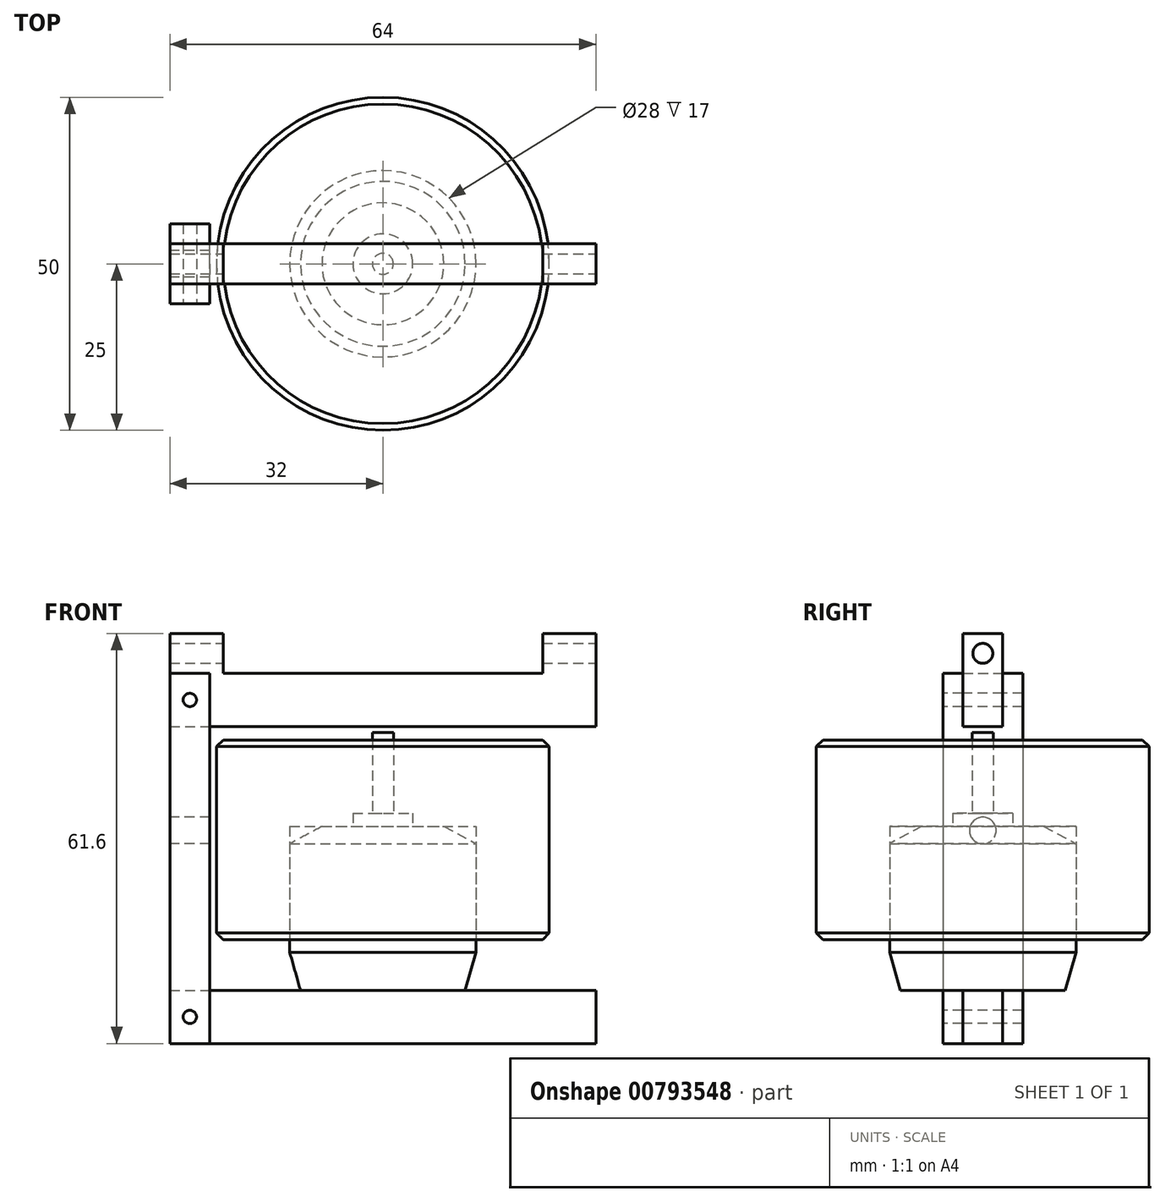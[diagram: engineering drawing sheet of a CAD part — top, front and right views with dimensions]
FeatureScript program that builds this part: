
annotation { "Feature Type Name" : "Feature", "Feature Type Description" : "" }
export const myFeature = defineFeature(function(context is Context, id is Id, definition is map)
    precondition{}
    {
        {
            var Q0;
            Q0=qCreatedBy(makeId("Right.planeOp"),FACE);
            var sketch = newSketch(context, id + "F0", { "sketchPlane" : qUnion([Q0])});
            skLineSegment(sketch, "E0", {"start": v(0, 0) * mm, "end": v(0, 26.6) * mm, "construction": true});
            skLineSegment(sketch, "E1", {"start": v(0, 26.6) * mm, "end": v(4.5, 26.6) * mm});
            skLineSegment(sketch, "E2", {"start": v(4.5, 26.6) * mm, "end": v(4.5, 24.6) * mm});
            skLineSegment(sketch, "E3", {"start": v(4.5, 24.6) * mm, "end": v(9.15, 24.6) * mm});
            skLineSegment(sketch, "E4", {"start": v(9.15, 24.6) * mm, "end": v(14, 22) * mm});
            skLineSegment(sketch, "E5", {"start": v(14, 22) * mm, "end": v(14, 5.7) * mm});
            skLineSegment(sketch, "E6", {"start": v(14, 5.7) * mm, "end": v(12.38, 0) * mm});
            skLineSegment(sketch, "E7", {"start": v(12.38, 0) * mm, "end": v(0, 0) * mm});
            skLineSegment(sketch, "E8", {"start": v(0, 26.6) * mm, "end": v(0, 0) * mm});
            skSolve(sketch);
        }
        {
            var Q0;
            Q0 = qSketchRegion(id + "F0", true);
            var Q1;
            Q1=sQuery(id+"F0.wireOp",EDGE,"E0");
            revolve(context, id + "F1", {"surfaceOperationType" : NewSurfaceOperationType.NEW, "entities" : qUnion([Q0]), "axis" : qUnion([Q1]), "revolveType" : RevolveType.FULL});
        }
        {
            var Q0;
            Q0=makeQuery(id+"F1.opRevolve","SWEPT_FACE",FACE,{"disambiguationData":[OSD([sQuery(id+"F0.wireOp",EDGE,"E1")])]});
            var sketch = newSketch(context, id + "F2", { "sketchPlane" : qUnion([Q0])});
            skCircle(sketch, "E9", {"center": v(0, 0) * mm, "radius": 1.59 * mm});
            skSolve(sketch);
        }
        {
            var Q0;
            Q0 = qSketchRegion(id + "F2", true);
            extrude(context, id + "F3", {"entities" : qUnion([Q0]), "operationType" : NewBodyOperationType.ADD, "depth" : 12.1 * mm, "offsetDistance" : 25 * mm});
        }
        {
            var Q0;
            Q0=qCreatedBy(makeId("Right.planeOp"),FACE);
            var sketch = newSketch(context, id + "F4", { "sketchPlane" : qUnion([Q0])});
            skLineSegment(sketch, "E10", {"start": v(0, 0) * mm, "end": v(0, 38.7) * mm, "construction": true});
            skLineSegment(sketch, "E11", {"start": v(1.58, 37.6) * mm, "end": v(1.59, 26.6) * mm});
            skLineSegment(sketch, "E12", {"start": v(1.59, 26.6) * mm, "end": v(4.5, 26.6) * mm});
            skLineSegment(sketch, "E13", {"start": v(14, 24.6) * mm, "end": v(14, 7.6) * mm});
            skLineSegment(sketch, "E14", {"start": v(14, 7.6) * mm, "end": v(25, 7.6) * mm});
            skLineSegment(sketch, "E15", {"start": v(25, 7.6) * mm, "end": v(25, 37.6) * mm});
            skLineSegment(sketch, "E16", {"start": v(25, 37.6) * mm, "end": v(1.58, 37.6) * mm});
            skLineSegment(sketch, "E17", {"start": v(4.5, 26.6) * mm, "end": v(4.5, 24.6) * mm});
            skLineSegment(sketch, "E18", {"start": v(4.5, 24.6) * mm, "end": v(14, 24.6) * mm});
            skSolve(sketch);
        }
        {
            var Q0;
            Q0 = qSketchRegion(id + "F4", true);
            var Q1;
            Q1=sQuery(id+"F4.wireOp",EDGE,"E10");
            revolve(context, id + "F5", {"surfaceOperationType" : NewSurfaceOperationType.NEW, "entities" : qUnion([Q0]), "axis" : qUnion([Q1]), "revolveType" : RevolveType.FULL});
        }
        {
            var Q0;
            Q0=makeQuery(id+"F5.opRevolve","SWEPT_EDGE",EDGE,{"disambiguationData":[OSD([sQuery(id+"F4.wireOp",EDGE,"E15"),sQuery(id+"F4.wireOp",EDGE,"E16")])]});
            var Q1;
            Q1=makeQuery(id+"F5.opRevolve","SWEPT_EDGE",EDGE,{"disambiguationData":[OSD([sQuery(id+"F4.wireOp",EDGE,"E14"),sQuery(id+"F4.wireOp",EDGE,"E15")])]});
            chamfer(context, id + "F6", {"entities" : qUnion([Q0, Q1]), "width" : 1 * mm, "tangentPropagation" : true});
        }
        {
            var Q0;
            Q0=qCreatedBy(makeId("Front.planeOp"),FACE);
            var sketch = newSketch(context, id + "F7", { "sketchPlane" : qUnion([Q0])});
            skLineSegment(sketch, "E19", {"start": v(-26, 36.6) * mm, "end": v(-26, 3) * mm});
            skLineSegment(sketch, "E20", {"start": v(-23, 0) * mm, "end": v(0, 0) * mm});
            skLineSegment(sketch, "E21", {"start": v(-32, 45.6) * mm, "end": v(-32, -6) * mm});
            skLineSegment(sketch, "E22", {"start": v(-32, -6) * mm, "end": v(0, -6) * mm});
            skLineSegment(sketch, "E23", {"start": v(0, 0) * mm, "end": v(0, -6) * mm, "construction": true});
            skLineSegment(sketch, "E24", {"start": v(-25, 8.6) * mm, "end": v(-25, 36.6) * mm, "construction": true});
            skLineSegment(sketch, "E25", {"start": v(-23, 39.6) * mm, "end": v(0, 39.6) * mm});
            skLineSegment(sketch, "E26", {"start": v(0, 39.6) * mm, "end": v(0, 45.6) * mm, "construction": true});
            skLineSegment(sketch, "E27", {"start": v(0, 45.6) * mm, "end": v(-32, 45.6) * mm});
            skLineSegment(sketch, "E28.MirrorCS", {"start": v(0, 45.6) * mm, "end": v(32, 45.6) * mm});
            skLineSegment(sketch, "E29.MirrorCS", {"start": v(25, 8.6) * mm, "end": v(25, 36.6) * mm, "construction": true});
            skLineSegment(sketch, "E30.MirrorCS", {"start": v(32, -6) * mm, "end": v(0, -6) * mm});
            skLineSegment(sketch, "E31.MirrorCS", {"start": v(32, 45.6) * mm, "end": v(32, -6) * mm});
            skLineSegment(sketch, "E32.MirrorCS", {"start": v(23, 39.6) * mm, "end": v(0, 39.6) * mm});
            skLineSegment(sketch, "E33.MirrorCS", {"start": v(23, 0) * mm, "end": v(0, 0) * mm});
            skLineSegment(sketch, "E34.MirrorCS", {"start": v(26, 36.6) * mm, "end": v(26, 3) * mm});
            skPoint(sketch, "E35.visualSharp", {"position": v(-26, 39.6) * mm});
            skArc(sketch, "E35.filletArc", {"start": v(-23, 39.6) * mm, "mid": v(-25.12, 38.72) * mm, "end": v(-26, 36.6) * mm});
            skPoint(sketch, "E36.visualSharp", {"position": v(26, 39.6) * mm});
            skArc(sketch, "E36.filletArc", {"start": v(26, 36.6) * mm, "mid": v(25.12, 38.72) * mm, "end": v(23, 39.6) * mm});
            skPoint(sketch, "E37.visualSharp", {"position": v(26, 0) * mm});
            skArc(sketch, "E37.filletArc", {"start": v(23, 0) * mm, "mid": v(25.12, 0.88) * mm, "end": v(26, 3) * mm});
            skPoint(sketch, "E38.visualSharp", {"position": v(-26, 0) * mm});
            skArc(sketch, "E38.filletArc", {"start": v(-26, 3) * mm, "mid": v(-25.12, 0.88) * mm, "end": v(-23, 0) * mm});
            skSolve(sketch);
        }
        {
            var Q0;
            Q0 = qSketchRegion(id + "F7", true);
            extrude(context, id + "F8", {"entities" : qUnion([Q0]), "endBound" : BoundingType.SYMMETRIC, "depth" : 12 * mm, "offsetDistance" : 25 * mm});
        }
        {
            var Q0;
            Q0=makeQuery(id+"F8.opExtrude","SWEPT_EDGE",EDGE,{"disambiguationData":[OSD([sQuery(id+"F7.wireOp",EDGE,"E21"),sQuery(id+"F7.wireOp",EDGE,"E27")])]});
            var Q1;
            Q1=makeQuery(id+"F8.opExtrude","SWEPT_EDGE",EDGE,{"disambiguationData":[OSD([sQuery(id+"F7.wireOp",EDGE,"E28.MirrorCS"),sQuery(id+"F7.wireOp",EDGE,"E31.MirrorCS")])]});
            var Q2;
            Q2=makeQuery(id+"F8.opExtrude","SWEPT_EDGE",EDGE,{"disambiguationData":[OSD([sQuery(id+"F7.wireOp",EDGE,"E21"),sQuery(id+"F7.wireOp",EDGE,"E22")])]});
            var Q3;
            Q3=makeQuery(id+"F8.opExtrude","SWEPT_EDGE",EDGE,{"disambiguationData":[OSD([sQuery(id+"F7.wireOp",EDGE,"E30.MirrorCS"),sQuery(id+"F7.wireOp",EDGE,"E31.MirrorCS")])]});
            chamfer(context, id + "F9", {"entities" : qUnion([Q0, Q1, Q2, Q3]), "width" : 3 * mm, "tangentPropagation" : true});
        }
        {
            var Q0;
            Q0=makeQuery(id+"F8.opExtrude","SWEPT_FACE",FACE,{"disambiguationData":[OSD([sQuery(id+"F7.wireOp",EDGE,"E31.MirrorCS")])]});
            var sketch = newSketch(context, id + "F10", { "sketchPlane" : qUnion([Q0])});
            skLineSegment(sketch, "E39", {"start": v(0, 0) * mm, "end": v(0, 24) * mm, "construction": true});
            skCircle(sketch, "E40", {"center": v(0, 24) * mm, "radius": 2.5 * mm});
            skSolve(sketch);
        }
        {
            var Q0;
            Q0 = qSketchRegion(id + "F10", true);
            extrude(context, id + "F11", {"entities" : qUnion([Q0]), "operationType" : NewBodyOperationType.REMOVE, "endBound" : BoundingType.UP_TO_NEXT, "oppositeDirection" : true, "depth" : 25 * mm, "offsetDistance" : 25 * mm});
        }
        {
            var Q0;
            Q0=makeQuery(id+"F8.opExtrude","SWEPT_BODY",BODY,{"disambiguationData":[OSD([sQuery(id+"F7.wireOp",EDGE,"E19"),sQuery(id+"F7.wireOp",EDGE,"E20"),sQuery(id+"F7.wireOp",EDGE,"E21"),sQuery(id+"F7.wireOp",EDGE,"E22"),sQuery(id+"F7.wireOp",EDGE,"E25"),sQuery(id+"F7.wireOp",EDGE,"E27"),sQuery(id+"F7.wireOp",EDGE,"E28.MirrorCS"),sQuery(id+"F7.wireOp",EDGE,"E30.MirrorCS"),sQuery(id+"F7.wireOp",EDGE,"E31.MirrorCS"),sQuery(id+"F7.wireOp",EDGE,"E32.MirrorCS"),sQuery(id+"F7.wireOp",EDGE,"E33.MirrorCS"),sQuery(id+"F7.wireOp",EDGE,"E34.MirrorCS"),sQuery(id+"F7.wireOp",EDGE,"E35.filletArc"),sQuery(id+"F7.wireOp",EDGE,"E36.filletArc"),sQuery(id+"F7.wireOp",EDGE,"E37.filletArc"),sQuery(id+"F7.wireOp",EDGE,"E38.filletArc")])]});
            deleteBodies(context, id + "F12", {"entities" : qUnion([Q0])});
        }
        {
            var Q0;
            Q0=qCreatedBy(makeId("Right.planeOp"),FACE);
            cPlane(context, id + "F13", {"entities" : qUnion([Q0]), "cplaneType" : CPlaneType.OFFSET, "offset" : 26 * mm, "oppositeDirection" : true, "width" : 150 * mm, "height" : 150 * mm});
        }
        {
            var Q0;
            Q0=qCreatedBy(id+"F13.planeOp",FACE);
            var sketch = newSketch(context, id + "F14", { "sketchPlane" : qUnion([Q0])});
            skLineSegment(sketch, "E41", {"start": v(0, 0) * mm, "end": v(0, 39.6) * mm, "construction": true});
            skLineSegment(sketch, "E42", {"start": v(0, 39.6) * mm, "end": v(3, 39.6) * mm});
            skLineSegment(sketch, "E43", {"start": v(3, 47.6) * mm, "end": v(3, 39.6) * mm});
            skLineSegment(sketch, "E44", {"start": v(3, 47.6) * mm, "end": v(6, 47.6) * mm});
            skLineSegment(sketch, "E45", {"start": v(6, 47.6) * mm, "end": v(6, -8) * mm});
            skLineSegment(sketch, "E46", {"start": v(6, -8) * mm, "end": v(3, -8) * mm});
            skLineSegment(sketch, "E47", {"start": v(3, 0) * mm, "end": v(3, -8) * mm});
            skLineSegment(sketch, "E48", {"start": v(3, 0) * mm, "end": v(0, 0) * mm});
            skLineSegment(sketch, "E49", {"start": v(0, 0) * mm, "end": v(0, 0) * mm});
            skLineSegment(sketch, "E50.MirrorCS", {"start": v(0, 39.6) * mm, "end": v(-3, 39.6) * mm});
            skLineSegment(sketch, "E51.MirrorCS", {"start": v(-3, 47.6) * mm, "end": v(-3, 39.6) * mm});
            skLineSegment(sketch, "E52.MirrorCS", {"start": v(-3, 47.6) * mm, "end": v(-6, 47.6) * mm});
            skLineSegment(sketch, "E53.MirrorCS", {"start": v(-6, 47.6) * mm, "end": v(-6, -8) * mm});
            skLineSegment(sketch, "E54.MirrorCS", {"start": v(-6, -8) * mm, "end": v(-3, -8) * mm});
            skLineSegment(sketch, "E55.MirrorCS", {"start": v(-3, 0) * mm, "end": v(-3, -8) * mm});
            skLineSegment(sketch, "E56.MirrorCS", {"start": v(-3, 0) * mm, "end": v(0, 0) * mm});
            skSolve(sketch);
        }
        {
            var Q0;
            Q0 = qSketchRegion(id + "F14", true);
            extrude(context, id + "F15", {"entities" : qUnion([Q0]), "operationType" : NewBodyOperationType.ADD, "oppositeDirection" : true, "depth" : 6 * mm, "offsetDistance" : 25 * mm});
        }
        {
            var Q0;
            Q0=makeQuery(id+"F15.opExtrude","SWEPT_FACE",FACE,{"disambiguationData":[OSD([sQuery(id+"F14.wireOp",EDGE,"E43")])]});
            var sketch = newSketch(context, id + "F16", { "sketchPlane" : qUnion([Q0])});
            skLineSegment(sketch, "E57.bottom", {"start": v(-32, 39.6) * mm, "end": v(0, 39.6) * mm});
            skLineSegment(sketch, "E57.top", {"start": v(-24, 47.6) * mm, "end": v(0, 47.6) * mm});
            skLineSegment(sketch, "E57.left", {"start": v(-32, 39.6) * mm, "end": v(-32, 53.6) * mm});
            skLineSegment(sketch, "E57.right", {"start": v(0, 39.6) * mm, "end": v(0, 47.6) * mm, "construction": true});
            skLineSegment(sketch, "E58.MirrorCS", {"start": v(24, 47.6) * mm, "end": v(0, 47.6) * mm});
            skLineSegment(sketch, "E59.MirrorCS", {"start": v(32, 39.6) * mm, "end": v(32, 53.6) * mm});
            skLineSegment(sketch, "E60.MirrorCS", {"start": v(32, 39.6) * mm, "end": v(0, 39.6) * mm});
            skLineSegment(sketch, "E61", {"start": v(-24, 47.6) * mm, "end": v(-24, 53.6) * mm});
            skLineSegment(sketch, "E62", {"start": v(-24, 53.6) * mm, "end": v(-32, 53.6) * mm});
            skPoint(sketch, "E63.orphan", {"position": v(-32, 47.6) * mm});
            skLineSegment(sketch, "E64", {"start": v(24, 53.6) * mm, "end": v(32, 53.6) * mm});
            skPoint(sketch, "E65.orphan", {"position": v(32, 47.6) * mm});
            skLineSegment(sketch, "E66", {"start": v(24, 47.6) * mm, "end": v(24, 53.6) * mm});
            skSolve(sketch);
        }
        {
            var Q0;
            Q0 = qSketchRegion(id + "F16", true);
            var Q1;
            Q1=makeQuery(id+"F15.opExtrude","SWEPT_FACE",FACE,{"disambiguationData":[OSD([sQuery(id+"F14.wireOp",EDGE,"E51.MirrorCS")])]});
            extrude(context, id + "F17", {"entities" : qUnion([Q0]), "endBound" : BoundingType.UP_TO_SURFACE, "depth" : 25 * mm, "endBoundEntityFace" : qUnion([Q1]), "offsetDistance" : 25 * mm});
        }
        {
            var Q0;
            Q0=makeQuery(id+"F15.opExtrude","SWEPT_FACE",FACE,{"disambiguationData":[OSD([sQuery(id+"F14.wireOp",EDGE,"E47")])]});
            var sketch = newSketch(context, id + "F18", { "sketchPlane" : qUnion([Q0])});
            skLineSegment(sketch, "E67.bottom", {"start": v(-32, 0) * mm, "end": v(0, 0) * mm});
            skLineSegment(sketch, "E67.left", {"start": v(-32, 0) * mm, "end": v(-32, -8) * mm});
            skLineSegment(sketch, "E67.right", {"start": v(0, 0) * mm, "end": v(0, -8) * mm, "construction": true});
            skLineSegment(sketch, "E68.MirrorCS", {"start": v(32, 0) * mm, "end": v(0, 0) * mm});
            skLineSegment(sketch, "E69.MirrorCS", {"start": v(32, 0) * mm, "end": v(32, -8) * mm});
            skLineSegment(sketch, "E70.MirrorCS", {"start": v(32, -8) * mm, "end": v(0, -8) * mm});
            skLineSegment(sketch, "E71.trimOffspring", {"start": v(-32, -8) * mm, "end": v(0, -8) * mm});
            skPoint(sketch, "E72.orphan", {"position": v(-32, -8) * mm});
            skSolve(sketch);
        }
        {
            var Q0;
            Q0 = qSketchRegion(id + "F18", true);
            var Q1;
            Q1=makeQuery(id+"F15.opExtrude","SWEPT_FACE",FACE,{"disambiguationData":[OSD([sQuery(id+"F14.wireOp",EDGE,"E55.MirrorCS")])]});
            extrude(context, id + "F19", {"entities" : qUnion([Q0]), "endBound" : BoundingType.UP_TO_SURFACE, "depth" : 25 * mm, "endBoundEntityFace" : qUnion([Q1]), "offsetDistance" : 25 * mm});
        }
        {
            var Q0;
            Q0=makeQuery(id+"F15.opExtrude","SWEPT_FACE",FACE,{"disambiguationData":[OSD([sQuery(id+"F14.wireOp",EDGE,"E53.MirrorCS")])]});
            var sketch = newSketch(context, id + "F20", { "sketchPlane" : qUnion([Q0])});
            skLineSegment(sketch, "E73", {"start": v(-26, 43.6) * mm, "end": v(-32, 43.6) * mm, "construction": true});
            skCircle(sketch, "E74", {"center": v(-29, 43.6) * mm, "radius": 1 * mm});
            skLineSegment(sketch, "E75", {"start": v(-32, -4) * mm, "end": v(-26, -4) * mm, "construction": true});
            skCircle(sketch, "E76", {"center": v(-29, -4) * mm, "radius": 1 * mm});
            skSolve(sketch);
        }
        {
            var Q0;
            Q0 = qSketchRegion(id + "F20", true);
            extrude(context, id + "F21", {"entities" : qUnion([Q0]), "operationType" : NewBodyOperationType.REMOVE, "endBound" : BoundingType.THROUGH_ALL, "oppositeDirection" : true, "depth" : 25 * mm, "offsetDistance" : 25 * mm});
        }
        {
            var Q0;
            Q0=makeQuery(id+"F15.opExtrude","CAP_FACE",FACE,{"disambiguationData":[OSD([sQuery(id+"F14.wireOp",EDGE,"E42"),sQuery(id+"F14.wireOp",EDGE,"E43"),sQuery(id+"F14.wireOp",EDGE,"E44"),sQuery(id+"F14.wireOp",EDGE,"E45"),sQuery(id+"F14.wireOp",EDGE,"E46"),sQuery(id+"F14.wireOp",EDGE,"E47"),sQuery(id+"F14.wireOp",EDGE,"E48"),sQuery(id+"F14.wireOp",EDGE,"E50.MirrorCS"),sQuery(id+"F14.wireOp",EDGE,"E51.MirrorCS"),sQuery(id+"F14.wireOp",EDGE,"E52.MirrorCS"),sQuery(id+"F14.wireOp",EDGE,"E53.MirrorCS"),sQuery(id+"F14.wireOp",EDGE,"E54.MirrorCS"),sQuery(id+"F14.wireOp",EDGE,"E55.MirrorCS"),sQuery(id+"F14.wireOp",EDGE,"E56.MirrorCS")])],"isStart":false});
            var sketch = newSketch(context, id + "F22", { "sketchPlane" : qUnion([Q0])});
            skLineSegment(sketch, "E77", {"start": v(0, 39.6) * mm, "end": v(0, 0) * mm, "construction": true});
            skCircle(sketch, "E78", {"center": v(0, 24) * mm, "radius": 2 * mm});
            skSolve(sketch);
        }
        {
            var Q0;
            Q0=makeQuery(id+"F22.imprint","IMPRINT",FACE,{"disambiguationData":[TD([[makeQuery(id+"F22.imprint","IMPRINT",EDGE,{"derivedFrom":sQuery(id+"F22.wireOp",EDGE,"E78")}),1.0]])]});
            extrude(context, id + "F23", {"entities" : qUnion([Q0]), "operationType" : NewBodyOperationType.REMOVE, "endBound" : BoundingType.UP_TO_NEXT, "oppositeDirection" : true, "depth" : 25 * mm, "offsetDistance" : 25 * mm});
        }
        {
            var Q0;
            Q0=makeQuery(id+"F17.opExtrude","SWEPT_FACE",FACE,{"disambiguationData":[OSD([sQuery(id+"F16.wireOp",EDGE,"E59.MirrorCS")])]});
            var sketch = newSketch(context, id + "F24", { "sketchPlane" : qUnion([Q0])});
            skLineSegment(sketch, "E79", {"start": v(0, 47.6) * mm, "end": v(0, 53.6) * mm, "construction": true});
            skCircle(sketch, "E80", {"center": v(0, 50.6) * mm, "radius": 1.5 * mm});
            skSolve(sketch);
        }
        {
            var Q0;
            Q0 = qSketchRegion(id + "F24", true);
            extrude(context, id + "F25", {"entities" : qUnion([Q0]), "operationType" : NewBodyOperationType.REMOVE, "endBound" : BoundingType.THROUGH_ALL, "oppositeDirection" : true, "depth" : 25 * mm, "offsetDistance" : 25 * mm});
        }
    });
